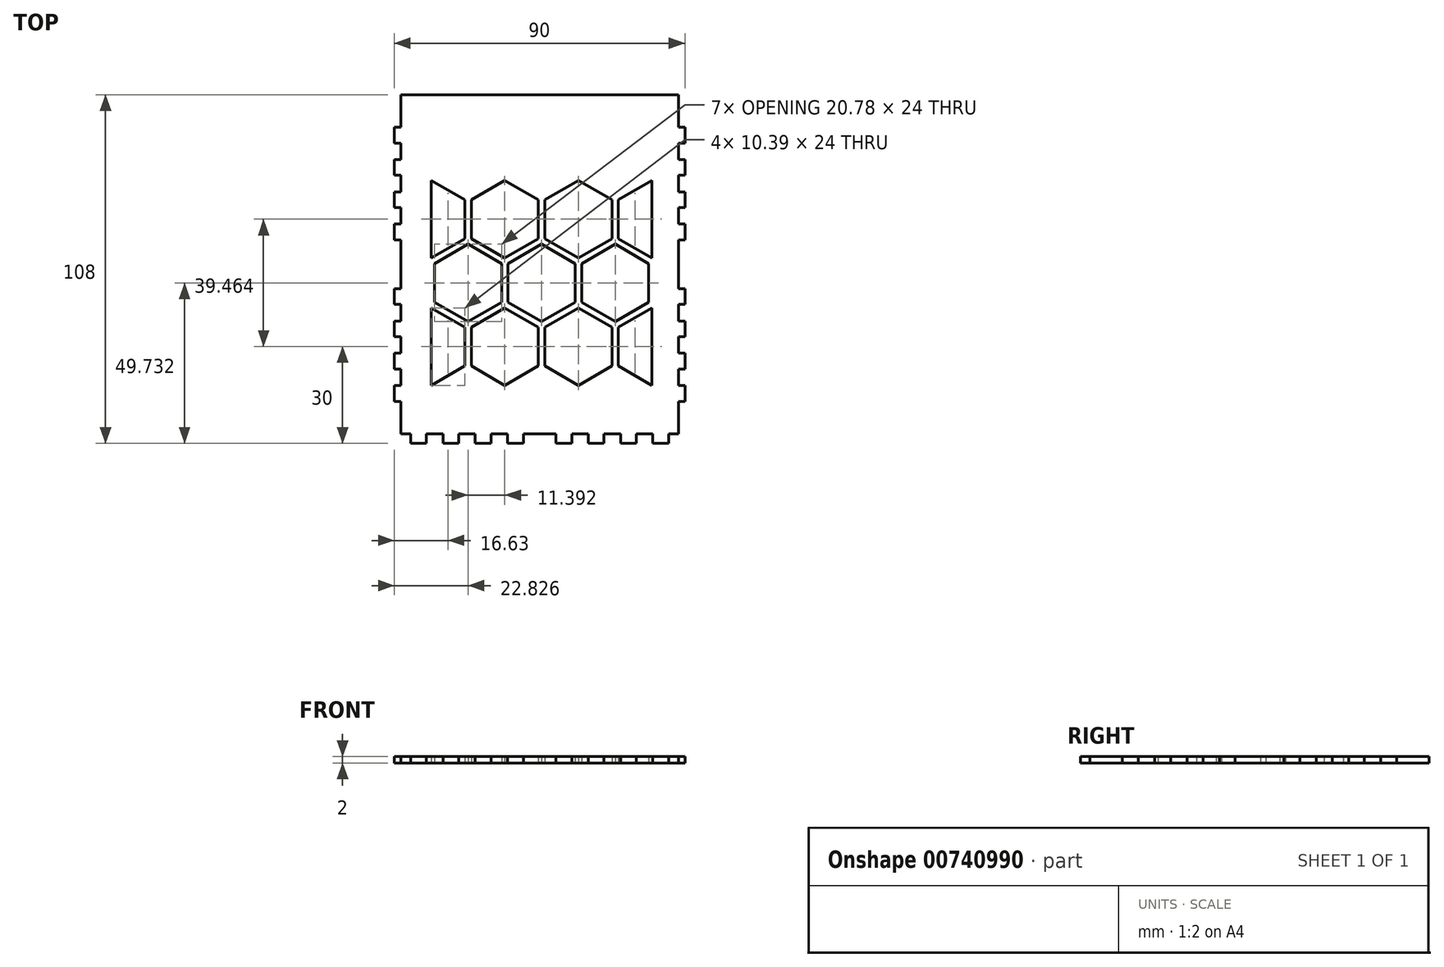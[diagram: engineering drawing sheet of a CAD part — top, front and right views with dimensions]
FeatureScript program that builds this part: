
annotation { "Feature Type Name" : "Feature", "Feature Type Description" : "" }
export const myFeature = defineFeature(function(context is Context, id is Id, definition is map)
    precondition{}
    {
        {
            var Q0;
            Q0=qCreatedBy(makeId("Top.planeOp"),FACE);
            var sketch = newSketch(context, id + "F0", { "sketchPlane" : qUnion([Q0])});
            skLineSegment(sketch, "E0.bottom", {"start": v(-43, 52.5) * mm, "end": v(43, 52.5) * mm});
            skLineSegment(sketch, "E0.top", {"start": v(-43, -52.5) * mm, "end": v(43, -52.5) * mm});
            skLineSegment(sketch, "E0.left", {"start": v(-43, 52.5) * mm, "end": v(-43, -52.5) * mm});
            skLineSegment(sketch, "E0.right", {"start": v(43, 52.5) * mm, "end": v(43, -52.5) * mm});
            skLineSegment(sketch, "E1", {"start": v(-43, 52.5) * mm, "end": v(43, -52.5) * mm, "construction": true});
            skLineSegment(sketch, "E2", {"start": v(43, 52.5) * mm, "end": v(-43, -52.5) * mm, "construction": true});
            skLineSegment(sketch, "E3.top", {"start": v(50.23, -52.5) * mm, "end": v(39.95, -52.5) * mm});
            skLineSegment(sketch, "E4.bottom", {"start": v(39.95, -55.5) * mm, "end": v(35.05, -55.5) * mm});
            skLineSegment(sketch, "E4.left", {"start": v(39.95, -55.5) * mm, "end": v(39.95, -52.5) * mm});
            skLineSegment(sketch, "E4.right", {"start": v(35.05, -55.5) * mm, "end": v(35.05, -52.5) * mm});
            skLineSegment(sketch, "E5.bottom", {"start": v(29.95, -55.5) * mm, "end": v(25.05, -55.5) * mm});
            skLineSegment(sketch, "E5.left", {"start": v(29.95, -55.5) * mm, "end": v(29.95, -52.5) * mm});
            skLineSegment(sketch, "E5.right", {"start": v(25.05, -55.5) * mm, "end": v(25.05, -52.5) * mm});
            skLineSegment(sketch, "E6.bottom", {"start": v(19.95, -55.5) * mm, "end": v(15.05, -55.5) * mm});
            skLineSegment(sketch, "E6.left", {"start": v(19.95, -55.5) * mm, "end": v(19.95, -52.5) * mm});
            skLineSegment(sketch, "E6.right", {"start": v(15.05, -55.5) * mm, "end": v(15.05, -52.5) * mm});
            skLineSegment(sketch, "E7.bottom", {"start": v(9.95, -55.5) * mm, "end": v(5.05, -55.5) * mm});
            skLineSegment(sketch, "E7.left", {"start": v(9.95, -55.5) * mm, "end": v(9.95, -52.5) * mm});
            skLineSegment(sketch, "E7.right", {"start": v(5.05, -55.5) * mm, "end": v(5.05, -52.5) * mm});
            skLineSegment(sketch, "E8.bottom", {"start": v(-5.05, -55.5) * mm, "end": v(-9.95, -55.5) * mm});
            skLineSegment(sketch, "E8.left", {"start": v(-5.05, -55.5) * mm, "end": v(-5.05, -52.5) * mm});
            skLineSegment(sketch, "E8.right", {"start": v(-9.95, -55.5) * mm, "end": v(-9.95, -52.5) * mm});
            skLineSegment(sketch, "E9.bottom", {"start": v(-15.05, -55.5) * mm, "end": v(-19.95, -55.5) * mm});
            skLineSegment(sketch, "E9.left", {"start": v(-15.05, -55.5) * mm, "end": v(-15.05, -52.5) * mm});
            skLineSegment(sketch, "E9.right", {"start": v(-19.95, -55.5) * mm, "end": v(-19.95, -52.5) * mm});
            skLineSegment(sketch, "E10.bottom", {"start": v(-25.05, -55.5) * mm, "end": v(-29.95, -55.5) * mm});
            skLineSegment(sketch, "E10.left", {"start": v(-25.05, -55.5) * mm, "end": v(-25.05, -52.5) * mm});
            skLineSegment(sketch, "E10.right", {"start": v(-29.95, -55.5) * mm, "end": v(-29.95, -52.5) * mm});
            skLineSegment(sketch, "E11.bottom", {"start": v(-35.05, -55.5) * mm, "end": v(-39.95, -55.5) * mm});
            skLineSegment(sketch, "E11.left", {"start": v(-35.05, -55.5) * mm, "end": v(-35.05, -52.5) * mm});
            skLineSegment(sketch, "E11.right", {"start": v(-39.95, -55.5) * mm, "end": v(-39.95, -52.5) * mm});
            skLineSegment(sketch, "E12.trimOffspring", {"start": v(-39.95, -52.5) * mm, "end": v(-43, -52.5) * mm});
            skLineSegment(sketch, "E13.trimOffspring", {"start": v(-29.95, -52.5) * mm, "end": v(-35.05, -52.5) * mm});
            skLineSegment(sketch, "E14.trimOffspring", {"start": v(-19.95, -52.5) * mm, "end": v(-25.05, -52.5) * mm});
            skLineSegment(sketch, "E15.trimOffspring", {"start": v(-9.95, -52.5) * mm, "end": v(-15.05, -52.5) * mm});
            skLineSegment(sketch, "E16.trimOffspring", {"start": v(5.05, -52.5) * mm, "end": v(-5.05, -52.5) * mm});
            skLineSegment(sketch, "E17.trimOffspring", {"start": v(15.05, -52.5) * mm, "end": v(9.95, -52.5) * mm});
            skLineSegment(sketch, "E18.trimOffspring", {"start": v(25.05, -52.5) * mm, "end": v(19.95, -52.5) * mm});
            skLineSegment(sketch, "E19.trimOffspring", {"start": v(35.05, -52.5) * mm, "end": v(29.95, -52.5) * mm});
            skLineSegment(sketch, "E20", {"start": v(-38.08, -55.5) * mm, "end": v(57, -55.5) * mm, "construction": true});
            skLineSegment(sketch, "E21.top", {"start": v(-43, -52.5) * mm, "end": v(-43, -42.45) * mm});
            skLineSegment(sketch, "E22.top", {"start": v(-45, 42.45) * mm, "end": v(-45, 37.55) * mm});
            skLineSegment(sketch, "E22.left", {"start": v(-43, 42.45) * mm, "end": v(-45, 42.45) * mm});
            skLineSegment(sketch, "E22.right", {"start": v(-43, 37.55) * mm, "end": v(-45, 37.55) * mm});
            skLineSegment(sketch, "E23.top", {"start": v(-45, 32.45) * mm, "end": v(-45, 27.55) * mm});
            skLineSegment(sketch, "E23.left", {"start": v(-43, 32.45) * mm, "end": v(-45, 32.45) * mm});
            skLineSegment(sketch, "E23.right", {"start": v(-43, 27.55) * mm, "end": v(-45, 27.55) * mm});
            skLineSegment(sketch, "E24.top", {"start": v(-45, 22.45) * mm, "end": v(-45, 17.55) * mm});
            skLineSegment(sketch, "E24.left", {"start": v(-43, 22.45) * mm, "end": v(-45, 22.45) * mm});
            skLineSegment(sketch, "E24.right", {"start": v(-43, 17.55) * mm, "end": v(-45, 17.55) * mm});
            skLineSegment(sketch, "E25.top", {"start": v(-45, 12.45) * mm, "end": v(-45, 7.55) * mm});
            skLineSegment(sketch, "E25.left", {"start": v(-43, 12.45) * mm, "end": v(-45, 12.45) * mm});
            skLineSegment(sketch, "E25.right", {"start": v(-43, 7.55) * mm, "end": v(-45, 7.55) * mm});
            skLineSegment(sketch, "E26.top", {"start": v(-45, -7.55) * mm, "end": v(-45, -12.45) * mm});
            skLineSegment(sketch, "E26.left", {"start": v(-43, -7.55) * mm, "end": v(-45, -7.55) * mm});
            skLineSegment(sketch, "E26.right", {"start": v(-43, -12.45) * mm, "end": v(-45, -12.45) * mm});
            skLineSegment(sketch, "E27.top", {"start": v(-45, -17.55) * mm, "end": v(-45, -22.45) * mm});
            skLineSegment(sketch, "E27.left", {"start": v(-43, -17.55) * mm, "end": v(-45, -17.55) * mm});
            skLineSegment(sketch, "E27.right", {"start": v(-43, -22.45) * mm, "end": v(-45, -22.45) * mm});
            skLineSegment(sketch, "E28.top", {"start": v(-45, -27.55) * mm, "end": v(-45, -32.45) * mm});
            skLineSegment(sketch, "E28.left", {"start": v(-43, -27.55) * mm, "end": v(-45, -27.55) * mm});
            skLineSegment(sketch, "E28.right", {"start": v(-43, -32.45) * mm, "end": v(-45, -32.45) * mm});
            skLineSegment(sketch, "E29.top", {"start": v(-45, -37.55) * mm, "end": v(-45, -42.45) * mm});
            skLineSegment(sketch, "E29.left", {"start": v(-43, -37.55) * mm, "end": v(-45, -37.55) * mm});
            skLineSegment(sketch, "E29.right", {"start": v(-43, -42.45) * mm, "end": v(-45, -42.45) * mm});
            skLineSegment(sketch, "E30.trimOffspring", {"start": v(-43, 37.55) * mm, "end": v(-43, 32.45) * mm});
            skLineSegment(sketch, "E31.trimOffspring", {"start": v(-43, 27.55) * mm, "end": v(-43, 22.45) * mm});
            skLineSegment(sketch, "E32.trimOffspring", {"start": v(-43, 17.55) * mm, "end": v(-43, 12.45) * mm});
            skLineSegment(sketch, "E33.trimOffspring", {"start": v(-43, 7.55) * mm, "end": v(-43, -7.55) * mm});
            skLineSegment(sketch, "E34.trimOffspring", {"start": v(-43, -12.45) * mm, "end": v(-43, -17.55) * mm});
            skLineSegment(sketch, "E35.trimOffspring", {"start": v(-43, -22.45) * mm, "end": v(-43, -27.55) * mm});
            skLineSegment(sketch, "E36.trimOffspring", {"start": v(-43, -32.45) * mm, "end": v(-43, -37.55) * mm});
            skLineSegment(sketch, "E37.trimOffspring", {"start": v(-43, -37.55) * mm, "end": v(-43, -32.45) * mm});
            skLineSegment(sketch, "E38.trimOffspring", {"start": v(-43, -17.55) * mm, "end": v(-43, -12.45) * mm});
            skLineSegment(sketch, "E39.trimOffspring", {"start": v(-43, -7.55) * mm, "end": v(-43, 7.55) * mm});
            skLineSegment(sketch, "E40.trimOffspring", {"start": v(-43, 12.45) * mm, "end": v(-43, 17.55) * mm});
            skLineSegment(sketch, "E41.trimOffspring", {"start": v(-43, 22.45) * mm, "end": v(-43, 27.55) * mm});
            skLineSegment(sketch, "E42.trimOffspring", {"start": v(-43, 32.45) * mm, "end": v(-43, 37.55) * mm});
            skLineSegment(sketch, "E43.trimOffspring", {"start": v(-43, 42.45) * mm, "end": v(-43, 52.5) * mm});
            skLineSegment(sketch, "E44", {"start": v(-45, 53.62) * mm, "end": v(-45, -56.87) * mm, "construction": true});
            skLineSegment(sketch, "E45.top", {"start": v(45, -42.45) * mm, "end": v(45, -37.55) * mm});
            skLineSegment(sketch, "E45.left", {"start": v(43, -42.45) * mm, "end": v(45, -42.45) * mm});
            skLineSegment(sketch, "E45.right", {"start": v(43, -37.55) * mm, "end": v(45, -37.55) * mm});
            skLineSegment(sketch, "E46.top", {"start": v(45, -32.45) * mm, "end": v(45, -27.55) * mm});
            skLineSegment(sketch, "E46.left", {"start": v(43, -32.45) * mm, "end": v(45, -32.45) * mm});
            skLineSegment(sketch, "E46.right", {"start": v(43, -27.55) * mm, "end": v(45, -27.55) * mm});
            skLineSegment(sketch, "E47.top", {"start": v(45, -22.45) * mm, "end": v(45, -17.55) * mm});
            skLineSegment(sketch, "E47.left", {"start": v(43, -22.45) * mm, "end": v(45, -22.45) * mm});
            skLineSegment(sketch, "E47.right", {"start": v(43, -17.55) * mm, "end": v(45, -17.55) * mm});
            skLineSegment(sketch, "E48.top", {"start": v(45, -12.45) * mm, "end": v(45, -7.55) * mm});
            skLineSegment(sketch, "E48.left", {"start": v(43, -12.45) * mm, "end": v(45, -12.45) * mm});
            skLineSegment(sketch, "E48.right", {"start": v(43, -7.55) * mm, "end": v(45, -7.55) * mm});
            skLineSegment(sketch, "E49.top", {"start": v(45, 7.55) * mm, "end": v(45, 12.45) * mm});
            skLineSegment(sketch, "E49.left", {"start": v(43, 7.55) * mm, "end": v(45, 7.55) * mm});
            skLineSegment(sketch, "E49.right", {"start": v(43, 12.45) * mm, "end": v(45, 12.45) * mm});
            skLineSegment(sketch, "E50.top", {"start": v(45, 17.55) * mm, "end": v(45, 22.45) * mm});
            skLineSegment(sketch, "E50.left", {"start": v(43, 17.55) * mm, "end": v(45, 17.55) * mm});
            skLineSegment(sketch, "E50.right", {"start": v(43, 22.45) * mm, "end": v(45, 22.45) * mm});
            skLineSegment(sketch, "E51.top", {"start": v(45, 27.55) * mm, "end": v(45, 32.45) * mm});
            skLineSegment(sketch, "E51.left", {"start": v(43, 27.55) * mm, "end": v(45, 27.55) * mm});
            skLineSegment(sketch, "E51.right", {"start": v(43, 32.45) * mm, "end": v(45, 32.45) * mm});
            skLineSegment(sketch, "E52.top", {"start": v(45, 37.55) * mm, "end": v(45, 42.45) * mm});
            skLineSegment(sketch, "E52.left", {"start": v(43, 37.55) * mm, "end": v(45, 37.55) * mm});
            skLineSegment(sketch, "E52.right", {"start": v(43, 42.45) * mm, "end": v(45, 42.45) * mm});
            skLineSegment(sketch, "E53.trimOffspring", {"start": v(43, -37.55) * mm, "end": v(43, -32.45) * mm});
            skLineSegment(sketch, "E54.trimOffspring", {"start": v(43, -27.55) * mm, "end": v(43, -22.45) * mm});
            skLineSegment(sketch, "E55.trimOffspring", {"start": v(43, -17.55) * mm, "end": v(43, -12.45) * mm});
            skLineSegment(sketch, "E56.trimOffspring", {"start": v(43, -7.55) * mm, "end": v(43, 7.55) * mm});
            skLineSegment(sketch, "E57.trimOffspring", {"start": v(43, 12.45) * mm, "end": v(43, 17.55) * mm});
            skLineSegment(sketch, "E58.trimOffspring", {"start": v(43, 22.45) * mm, "end": v(43, 27.55) * mm});
            skLineSegment(sketch, "E59.trimOffspring", {"start": v(43, 32.45) * mm, "end": v(43, 37.55) * mm});
            skLineSegment(sketch, "E60.trimOffspring", {"start": v(43, 37.55) * mm, "end": v(43, 32.45) * mm});
            skLineSegment(sketch, "E61.trimOffspring", {"start": v(43, 17.55) * mm, "end": v(43, 12.45) * mm});
            skLineSegment(sketch, "E62.trimOffspring", {"start": v(43, 7.55) * mm, "end": v(43, -7.55) * mm});
            skLineSegment(sketch, "E63.trimOffspring", {"start": v(43, -12.45) * mm, "end": v(43, -17.55) * mm});
            skLineSegment(sketch, "E64.trimOffspring", {"start": v(43, -22.45) * mm, "end": v(43, -27.55) * mm});
            skLineSegment(sketch, "E65.trimOffspring", {"start": v(43, -32.45) * mm, "end": v(43, -37.55) * mm});
            skLineSegment(sketch, "E66", {"start": v(45, 49.06) * mm, "end": v(45, -47.01) * mm, "construction": true});
            skSolve(sketch);
        }
        {
            var Q0;
            {var subQ18=sQuery(id+"F0.wireOp",EDGE,"E0.bottom");Q0=makeQuery(id+"F0.imprint","IMPRINT",FACE,{"disambiguationData":[TD([[makeQuery(id+"F0.imprint","IMPRINT",EDGE,{"derivedFrom":subQ18}),-1.0]])]});}
            var sketch = newSketch(context, id + "F1", { "sketchPlane" : qUnion([Q0])});
            skLineSegment(sketch, "E67", {"start": v(-135.1, 25.96) * mm, "end": v(-135.1, -64.04) * mm, "construction": true});
            skLineSegment(sketch, "E68", {"start": v(-135.1, 25.96) * mm, "end": v(124.9, 25.96) * mm, "construction": true});
            skLineSegment(sketch, "E69", {"start": v(90.9, 25.96) * mm, "end": v(90.9, -64.04) * mm});
            skLineSegment(sketch, "E70.0", {"start": v(-23.17, 7.96) * mm, "end": v(-33.57, 1.96) * mm});
            skLineSegment(sketch, "E70.4", {"start": v(-33.57, 25.96) * mm, "end": v(-23.17, 19.96) * mm});
            skLineSegment(sketch, "E70.5", {"start": v(-23.17, 19.96) * mm, "end": v(-23.17, 7.96) * mm});
            skCircle(sketch, "E71.cCircle", {"center": v(-10.78, 13.96) * mm, "radius": 10.4 * mm, "construction": true});
            skLineSegment(sketch, "E71.0", {"start": v(-0.39, 7.96) * mm, "end": v(-10.78, 1.96) * mm});
            skLineSegment(sketch, "E71.1", {"start": v(-10.78, 1.96) * mm, "end": v(-21.17, 7.96) * mm});
            skLineSegment(sketch, "E71.2", {"start": v(-21.17, 7.96) * mm, "end": v(-21.17, 19.96) * mm});
            skLineSegment(sketch, "E71.3", {"start": v(-21.17, 19.96) * mm, "end": v(-10.78, 25.96) * mm});
            skLineSegment(sketch, "E71.4", {"start": v(-10.78, 25.96) * mm, "end": v(-0.39, 19.96) * mm});
            skLineSegment(sketch, "E71.5", {"start": v(-0.39, 19.96) * mm, "end": v(-0.39, 7.96) * mm});
            skPoint(sketch, "E71.0.midPoint", {"position": v(-5.59, 4.96) * mm});
            skCircle(sketch, "E72.cCircle", {"center": v(12, 13.96) * mm, "radius": 10.4 * mm, "construction": true});
            skLineSegment(sketch, "E72.0", {"start": v(22.4, 7.96) * mm, "end": v(12, 1.96) * mm});
            skLineSegment(sketch, "E72.1", {"start": v(12, 1.96) * mm, "end": v(1.61, 7.96) * mm});
            skLineSegment(sketch, "E72.2", {"start": v(1.61, 7.96) * mm, "end": v(1.61, 19.96) * mm});
            skLineSegment(sketch, "E72.3", {"start": v(1.61, 19.96) * mm, "end": v(12, 25.96) * mm});
            skLineSegment(sketch, "E72.4", {"start": v(12, 25.96) * mm, "end": v(22.4, 19.96) * mm});
            skLineSegment(sketch, "E72.5", {"start": v(22.4, 19.96) * mm, "end": v(22.4, 7.96) * mm});
            skPoint(sketch, "E72.0.midPoint", {"position": v(17.2, 4.96) * mm});
            skLineSegment(sketch, "E73.1", {"start": v(34.79, 1.96) * mm, "end": v(24.4, 7.96) * mm});
            skLineSegment(sketch, "E73.2", {"start": v(24.4, 7.96) * mm, "end": v(24.4, 19.96) * mm});
            skLineSegment(sketch, "E73.3", {"start": v(24.4, 19.96) * mm, "end": v(34.79, 25.96) * mm});
            skCircle(sketch, "E74.cCircle", {"center": v(-22.17, -5.77) * mm, "radius": 10.4 * mm, "construction": true});
            skLineSegment(sketch, "E74.0", {"start": v(-11.78, -11.77) * mm, "end": v(-22.17, -17.77) * mm});
            skLineSegment(sketch, "E74.1", {"start": v(-22.17, -17.77) * mm, "end": v(-32.57, -11.77) * mm});
            skLineSegment(sketch, "E74.3", {"start": v(-32.57, 0.23) * mm, "end": v(-22.17, 6.23) * mm});
            skLineSegment(sketch, "E74.4", {"start": v(-22.17, 6.23) * mm, "end": v(-11.78, 0.23) * mm});
            skLineSegment(sketch, "E74.5", {"start": v(-11.78, 0.23) * mm, "end": v(-11.78, -11.77) * mm});
            skPoint(sketch, "E74.0.midPoint", {"position": v(-16.98, -14.77) * mm});
            skCircle(sketch, "E75.cCircle", {"center": v(0.61, -5.77) * mm, "radius": 10.4 * mm, "construction": true});
            skLineSegment(sketch, "E75.0", {"start": v(11, -11.77) * mm, "end": v(0.61, -17.77) * mm});
            skLineSegment(sketch, "E75.1", {"start": v(0.61, -17.77) * mm, "end": v(-9.78, -11.77) * mm});
            skLineSegment(sketch, "E75.2", {"start": v(-9.78, -11.77) * mm, "end": v(-9.78, 0.23) * mm});
            skLineSegment(sketch, "E75.3", {"start": v(-9.78, 0.23) * mm, "end": v(0.61, 6.23) * mm});
            skLineSegment(sketch, "E75.4", {"start": v(0.61, 6.23) * mm, "end": v(11, 0.23) * mm});
            skLineSegment(sketch, "E75.5", {"start": v(11, 0.23) * mm, "end": v(11, -11.77) * mm});
            skPoint(sketch, "E75.0.midPoint", {"position": v(5.8, -14.77) * mm});
            skCircle(sketch, "E76.cCircle", {"center": v(23.4, -5.77) * mm, "radius": 10.4 * mm, "construction": true});
            skLineSegment(sketch, "E76.0", {"start": v(33.79, -11.77) * mm, "end": v(23.4, -17.77) * mm});
            skLineSegment(sketch, "E76.1", {"start": v(23.4, -17.77) * mm, "end": v(13, -11.77) * mm});
            skLineSegment(sketch, "E76.2", {"start": v(13, -11.77) * mm, "end": v(13, 0.23) * mm});
            skLineSegment(sketch, "E76.3", {"start": v(13, 0.23) * mm, "end": v(23.4, 6.23) * mm});
            skLineSegment(sketch, "E76.4", {"start": v(23.4, 6.23) * mm, "end": v(33.79, 0.23) * mm});
            skLineSegment(sketch, "E76.5", {"start": v(33.79, 0.23) * mm, "end": v(33.79, -11.77) * mm});
            skPoint(sketch, "E76.0.midPoint", {"position": v(28.6, -14.77) * mm});
            skLineSegment(sketch, "E77", {"start": v(124.9, 6.23) * mm, "end": v(-135.1, 6.23) * mm, "construction": true});
            skLineSegment(sketch, "E78", {"start": v(-139.1, -17.77) * mm, "end": v(126.13, -17.77) * mm, "construction": true});
            skLineSegment(sketch, "E79", {"start": v(-135.1, -13.5) * mm, "end": v(124.9, -13.5) * mm, "construction": true});
            skLineSegment(sketch, "E80", {"start": v(-135.1, -37.5) * mm, "end": v(124.9, -37.5) * mm, "construction": true});
            skLineSegment(sketch, "E81.0", {"start": v(-23.17, -31.5) * mm, "end": v(-33.57, -37.5) * mm});
            skLineSegment(sketch, "E81.4", {"start": v(-33.57, -13.5) * mm, "end": v(-23.17, -19.5) * mm});
            skLineSegment(sketch, "E81.5", {"start": v(-23.17, -19.5) * mm, "end": v(-23.17, -31.5) * mm});
            skCircle(sketch, "E82.cCircle", {"center": v(-10.78, -25.5) * mm, "radius": 10.4 * mm, "construction": true});
            skLineSegment(sketch, "E82.0", {"start": v(-0.39, -31.5) * mm, "end": v(-10.78, -37.5) * mm});
            skLineSegment(sketch, "E82.1", {"start": v(-10.78, -37.5) * mm, "end": v(-21.17, -31.5) * mm});
            skLineSegment(sketch, "E82.2", {"start": v(-21.17, -31.5) * mm, "end": v(-21.17, -19.5) * mm});
            skLineSegment(sketch, "E82.3", {"start": v(-21.17, -19.5) * mm, "end": v(-10.78, -13.5) * mm});
            skLineSegment(sketch, "E82.4", {"start": v(-10.78, -13.5) * mm, "end": v(-0.39, -19.5) * mm});
            skLineSegment(sketch, "E82.5", {"start": v(-0.39, -19.5) * mm, "end": v(-0.39, -31.5) * mm});
            skPoint(sketch, "E82.0.midPoint", {"position": v(-5.59, -34.5) * mm});
            skCircle(sketch, "E83.cCircle", {"center": v(12, -25.5) * mm, "radius": 10.4 * mm, "construction": true});
            skLineSegment(sketch, "E83.0", {"start": v(22.4, -31.5) * mm, "end": v(12, -37.5) * mm});
            skLineSegment(sketch, "E83.1", {"start": v(12, -37.5) * mm, "end": v(1.61, -31.5) * mm});
            skLineSegment(sketch, "E83.2", {"start": v(1.61, -31.5) * mm, "end": v(1.61, -19.5) * mm});
            skLineSegment(sketch, "E83.3", {"start": v(1.61, -19.5) * mm, "end": v(12, -13.5) * mm});
            skLineSegment(sketch, "E83.4", {"start": v(12, -13.5) * mm, "end": v(22.4, -19.5) * mm});
            skLineSegment(sketch, "E83.5", {"start": v(22.4, -19.5) * mm, "end": v(22.4, -31.5) * mm});
            skPoint(sketch, "E83.0.midPoint", {"position": v(17.2, -34.5) * mm});
            skLineSegment(sketch, "E84.1", {"start": v(34.79, -37.5) * mm, "end": v(24.4, -31.5) * mm});
            skLineSegment(sketch, "E84.2", {"start": v(24.4, -31.5) * mm, "end": v(24.4, -19.5) * mm});
            skLineSegment(sketch, "E84.3", {"start": v(24.4, -19.5) * mm, "end": v(34.79, -13.5) * mm});
            skLineSegment(sketch, "E85", {"start": v(-33.57, 25.96) * mm, "end": v(-33.57, -37.5) * mm});
            skLineSegment(sketch, "E86", {"start": v(-32.57, 0.23) * mm, "end": v(-32.57, -11.77) * mm});
            skLineSegment(sketch, "E87", {"start": v(34.79, 25.96) * mm, "end": v(34.79, -37.5) * mm});
            skSolve(sketch);
        }
        {
            var Q0;
            {var subQ47=sQuery(id+"F0.wireOp",EDGE,"E0.bottom");Q0=qUnion([makeQuery(id+"F0.imprint","IMPRINT",FACE,{"disambiguationData":[TD([[makeQuery(id+"F0.imprint","IMPRINT",EDGE,{"derivedFrom":sQuery(id+"F0.wireOp",EDGE,"E47.top")}),1.0]])]}),makeQuery(id+"F0.imprint","IMPRINT",FACE,{"disambiguationData":[TD([[makeQuery(id+"F0.imprint","IMPRINT",EDGE,{"derivedFrom":sQuery(id+"F0.wireOp",EDGE,"E8.bottom")}),-1.0]])]}),makeQuery(id+"F0.imprint","IMPRINT",FACE,{"disambiguationData":[TD([[makeQuery(id+"F0.imprint","IMPRINT",EDGE,{"derivedFrom":sQuery(id+"F0.wireOp",EDGE,"E51.top")}),1.0]])]}),makeQuery(id+"F0.imprint","IMPRINT",FACE,{"disambiguationData":[TD([[makeQuery(id+"F0.imprint","IMPRINT",EDGE,{"derivedFrom":sQuery(id+"F0.wireOp",EDGE,"E6.bottom")}),-1.0]])]}),makeQuery(id+"F0.imprint","IMPRINT",FACE,{"disambiguationData":[TD([[makeQuery(id+"F0.imprint","IMPRINT",EDGE,{"derivedFrom":sQuery(id+"F0.wireOp",EDGE,"E50.top")}),1.0]])]}),makeQuery(id+"F0.imprint","IMPRINT",FACE,{"disambiguationData":[TD([[makeQuery(id+"F0.imprint","IMPRINT",EDGE,{"derivedFrom":sQuery(id+"F0.wireOp",EDGE,"E23.top")}),1.0]])]}),makeQuery(id+"F0.imprint","IMPRINT",FACE,{"disambiguationData":[TD([[makeQuery(id+"F0.imprint","IMPRINT",EDGE,{"derivedFrom":sQuery(id+"F0.wireOp",EDGE,"E28.top")}),1.0]])]}),makeQuery(id+"F0.imprint","IMPRINT",FACE,{"disambiguationData":[TD([[makeQuery(id+"F0.imprint","IMPRINT",EDGE,{"derivedFrom":sQuery(id+"F0.wireOp",EDGE,"E49.top")}),1.0]])]}),makeQuery(id+"F0.imprint","IMPRINT",FACE,{"disambiguationData":[TD([[makeQuery(id+"F0.imprint","IMPRINT",EDGE,{"derivedFrom":sQuery(id+"F0.wireOp",EDGE,"E22.top")}),1.0]])]}),makeQuery(id+"F0.imprint","IMPRINT",FACE,{"disambiguationData":[TD([[makeQuery(id+"F0.imprint","IMPRINT",EDGE,{"derivedFrom":sQuery(id+"F0.wireOp",EDGE,"E29.top")}),1.0]])]}),makeQuery(id+"F0.imprint","IMPRINT",FACE,{"disambiguationData":[TD([[makeQuery(id+"F0.imprint","IMPRINT",EDGE,{"derivedFrom":sQuery(id+"F0.wireOp",EDGE,"E48.top")}),1.0]])]}),makeQuery(id+"F0.imprint","IMPRINT",FACE,{"disambiguationData":[TD([[makeQuery(id+"F0.imprint","IMPRINT",EDGE,{"derivedFrom":sQuery(id+"F0.wireOp",EDGE,"E24.top")}),1.0]])]}),makeQuery(id+"F0.imprint","IMPRINT",FACE,{"disambiguationData":[TD([[makeQuery(id+"F0.imprint","IMPRINT",EDGE,{"derivedFrom":sQuery(id+"F0.wireOp",EDGE,"E27.top")}),1.0]])]}),makeQuery(id+"F0.imprint","IMPRINT",FACE,{"disambiguationData":[TD([[makeQuery(id+"F0.imprint","IMPRINT",EDGE,{"derivedFrom":sQuery(id+"F0.wireOp",EDGE,"E52.top")}),1.0]])]}),makeQuery(id+"F0.imprint","IMPRINT",FACE,{"disambiguationData":[TD([[makeQuery(id+"F0.imprint","IMPRINT",EDGE,{"derivedFrom":sQuery(id+"F0.wireOp",EDGE,"E25.top")}),1.0]])]}),makeQuery(id+"F0.imprint","IMPRINT",FACE,{"disambiguationData":[TD([[makeQuery(id+"F0.imprint","IMPRINT",EDGE,{"derivedFrom":sQuery(id+"F0.wireOp",EDGE,"E26.top")}),1.0]])]}),makeQuery(id+"F0.imprint","IMPRINT",FACE,{"disambiguationData":[TD([[makeQuery(id+"F0.imprint","IMPRINT",EDGE,{"derivedFrom":sQuery(id+"F0.wireOp",EDGE,"E10.bottom")}),-1.0]])]}),makeQuery(id+"F0.imprint","IMPRINT",FACE,{"disambiguationData":[TD([[makeQuery(id+"F0.imprint","IMPRINT",EDGE,{"derivedFrom":sQuery(id+"F0.wireOp",EDGE,"E7.bottom")}),-1.0]])]}),makeQuery(id+"F0.imprint","IMPRINT",FACE,{"disambiguationData":[TD([[makeQuery(id+"F0.imprint","IMPRINT",EDGE,{"derivedFrom":sQuery(id+"F0.wireOp",EDGE,"E9.bottom")}),-1.0]])]}),makeQuery(id+"F0.imprint","IMPRINT",FACE,{"disambiguationData":[TD([[makeQuery(id+"F0.imprint","IMPRINT",EDGE,{"derivedFrom":sQuery(id+"F0.wireOp",EDGE,"E11.bottom")}),-1.0]])]}),makeQuery(id+"F0.imprint","IMPRINT",FACE,{"disambiguationData":[TD([[makeQuery(id+"F0.imprint","IMPRINT",EDGE,{"derivedFrom":subQ47}),-1.0]])]}),makeQuery(id+"F0.imprint","IMPRINT",FACE,{"disambiguationData":[TD([[makeQuery(id+"F0.imprint","IMPRINT",EDGE,{"derivedFrom":sQuery(id+"F0.wireOp",EDGE,"E5.bottom")}),-1.0]])]}),makeQuery(id+"F0.imprint","IMPRINT",FACE,{"disambiguationData":[TD([[makeQuery(id+"F0.imprint","IMPRINT",EDGE,{"derivedFrom":sQuery(id+"F0.wireOp",EDGE,"E46.top")}),1.0]])]}),makeQuery(id+"F0.imprint","IMPRINT",FACE,{"disambiguationData":[TD([[makeQuery(id+"F0.imprint","IMPRINT",EDGE,{"derivedFrom":sQuery(id+"F0.wireOp",EDGE,"E4.bottom")}),-1.0]])]}),makeQuery(id+"F0.imprint","IMPRINT",FACE,{"disambiguationData":[TD([[makeQuery(id+"F0.imprint","IMPRINT",EDGE,{"derivedFrom":sQuery(id+"F0.wireOp",EDGE,"E45.top")}),1.0]])]})]);}
            extrude(context, id + "F2", {"entities" : qUnion([Q0]), "depth" : 2 * mm, "offsetDistance" : 25 * mm});
        }
        {
            var Q0;
            Q0 = qSketchRegion(id + "F1", true);
            extrude(context, id + "F3", {"entities" : qUnion([Q0]), "operationType" : NewBodyOperationType.REMOVE, "endBound" : BoundingType.SYMMETRIC, "depth" : 25 * mm, "offsetDistance" : 25 * mm});
        }
    });
